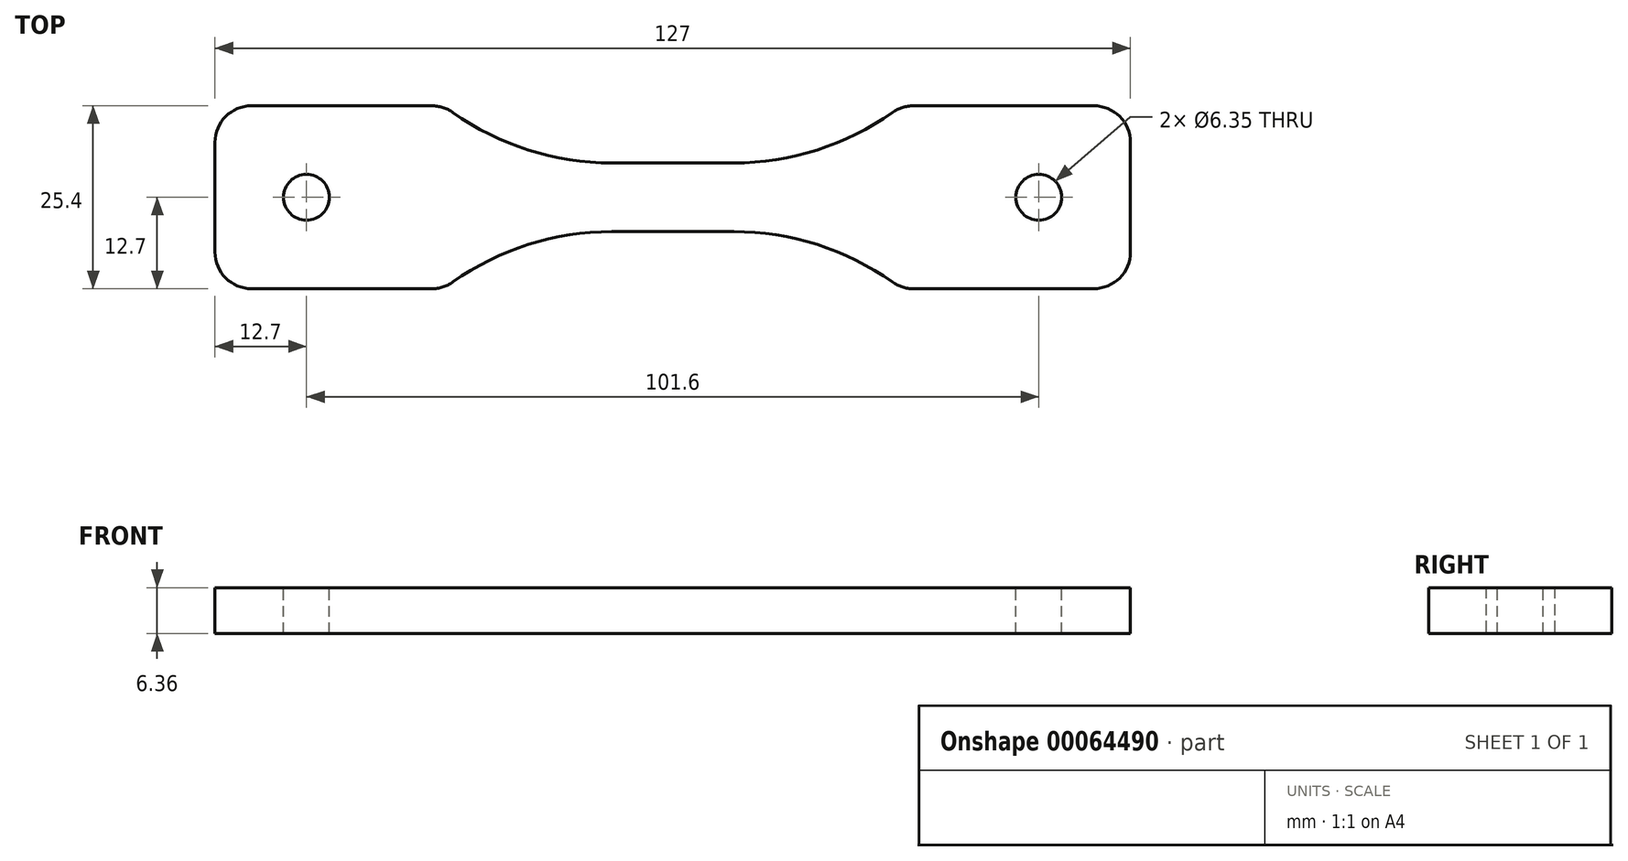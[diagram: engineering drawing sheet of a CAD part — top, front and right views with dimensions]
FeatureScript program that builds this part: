
annotation { "Feature Type Name" : "Feature", "Feature Type Description" : "" }
export const myFeature = defineFeature(function(context is Context, id is Id, definition is map)
    precondition{}
    {
        {
            var Q0;
            Q0=qCreatedBy(makeId("Top.planeOp"),FACE);
            var sketch = newSketch(context, id + "F0", { "sketchPlane" : qUnion([Q0])});
            skLineSegment(sketch, "E0.rect.bottom", {"start": v(63.5, -12.7) * mm, "end": v(-63.5, -12.7) * mm});
            skLineSegment(sketch, "E0.rect.top", {"start": v(63.5, 12.7) * mm, "end": v(-63.5, 12.7) * mm});
            skLineSegment(sketch, "E0.rect.left", {"start": v(63.5, -12.7) * mm, "end": v(63.5, 12.7) * mm});
            skLineSegment(sketch, "E0.rect.right", {"start": v(-63.5, -12.7) * mm, "end": v(-63.5, 12.7) * mm});
            skPoint(sketch, "E0.rect.middle", {"position": v(0, 0) * mm});
            skSolve(sketch);
        }
        {
            var Q0;
            Q0=makeQuery(id+"F0.imprint","IMPRINT",FACE,{"disambiguationData":[TD([[makeQuery(id+"F0.imprint","IMPRINT",EDGE,{"derivedFrom":sQuery(id+"F0.wireOp",EDGE,"E0.rect.bottom")}),-1.0]])]});
            extrude(context, id + "F1", {"entities" : qUnion([Q0]), "endBound" : BoundingType.SYMMETRIC, "depth" : 6.35 * mm});
        }
        {
            var Q0;
            Q0=makeQuery(id+"F1.opExtrude","CAP_FACE",FACE,{"disambiguationData":[OSD([sQuery(id+"F0.wireOp",EDGE,"E0.rect.bottom"),sQuery(id+"F0.wireOp",EDGE,"E0.rect.top"),sQuery(id+"F0.wireOp",EDGE,"E0.rect.left"),sQuery(id+"F0.wireOp",EDGE,"E0.rect.right")])],"isStart":false});
            var sketch = newSketch(context, id + "F2", { "sketchPlane" : qUnion([Q0])});
            skLineSegment(sketch, "E1", {"start": v(0, 50.7) * mm, "end": v(0, -34.35) * mm, "construction": true});
            skLineSegment(sketch, "E2.rect.bottom", {"start": v(31.75, 12.7) * mm, "end": v(-31.75, 12.7) * mm});
            skLineSegment(sketch, "E2.rect.top", {"start": v(31.75, 4.76) * mm, "end": v(-31.75, 4.76) * mm});
            skLineSegment(sketch, "E2.rect.left", {"start": v(31.75, 12.7) * mm, "end": v(31.75, 4.76) * mm});
            skLineSegment(sketch, "E2.rect.right", {"start": v(-31.75, 12.7) * mm, "end": v(-31.75, 4.76) * mm});
            skPoint(sketch, "E2.rect.middle", {"position": v(0, 8.73) * mm});
            skLineSegment(sketch, "E3", {"start": v(-70.63, 0) * mm, "end": v(74, 0) * mm, "construction": true});
            skPoint(sketch, "E3.endSnap0", {"position": v(-63.5, 0) * mm});
            skLineSegment(sketch, "E4.MirrorCS", {"start": v(-31.75, -12.7) * mm, "end": v(-31.75, -4.76) * mm});
            skPoint(sketch, "E5.MirrorP", {"position": v(0, -8.73) * mm});
            skLineSegment(sketch, "E6.MirrorCS", {"start": v(31.75, -12.7) * mm, "end": v(-31.75, -12.7) * mm});
            skLineSegment(sketch, "E7.MirrorCS", {"start": v(31.75, -4.76) * mm, "end": v(-31.75, -4.76) * mm});
            skLineSegment(sketch, "E8.MirrorCS", {"start": v(31.75, -12.7) * mm, "end": v(31.75, -4.76) * mm});
            skSolve(sketch);
        }
        {
            var Q0;
            Q0 = qSketchRegion(id + "F2", true);
            extrude(context, id + "F3", {"entities" : qUnion([Q0]), "operationType" : NewBodyOperationType.REMOVE, "oppositeDirection" : true, "depth" : 25.4 * mm});
        }
        {
            var Q0;
            Q0=makeQuery(id+"F3.boolean.opBoolean","COPY",EDGE,{"derivedFrom":makeQuery(id+"F3.opExtrude","SWEPT_EDGE",EDGE,{"disambiguationData":[OSD([sQuery(id+"F2.wireOp",EDGE,"E2.rect.top"),sQuery(id+"F2.wireOp",EDGE,"E2.rect.right")])]})});
            var Q1;
            Q1=makeQuery(id+"F3.boolean.opBoolean","COPY",EDGE,{"derivedFrom":makeQuery(id+"F3.opExtrude","SWEPT_EDGE",EDGE,{"disambiguationData":[OSD([sQuery(id+"F2.wireOp",EDGE,"E2.rect.top"),sQuery(id+"F2.wireOp",EDGE,"E2.rect.left")])]})});
            var Q2;
            Q2=makeQuery(id+"F3.boolean.opBoolean","COPY",EDGE,{"derivedFrom":makeQuery(id+"F3.opExtrude","SWEPT_EDGE",EDGE,{"disambiguationData":[OSD([sQuery(id+"F2.wireOp",EDGE,"E7.MirrorCS"),sQuery(id+"F2.wireOp",EDGE,"E8.MirrorCS")])]})});
            var Q3;
            Q3=makeQuery(id+"F3.boolean.opBoolean","COPY",EDGE,{"derivedFrom":makeQuery(id+"F3.opExtrude","SWEPT_EDGE",EDGE,{"disambiguationData":[OSD([sQuery(id+"F2.wireOp",EDGE,"E4.MirrorCS"),sQuery(id+"F2.wireOp",EDGE,"E7.MirrorCS")])]})});
            fillet(context, id + "F4", {"entities" : qUnion([Q0, Q1, Q2, Q3]), "radius" : 38.1 * mm, "tangentPropagation" : true, "allowEdgeOverflow" : false});
        }
        {
            var Q0;
            Q0=makeQuery(id+"F1.opExtrude","SWEPT_EDGE",EDGE,{"disambiguationData":[OSD([sQuery(id+"F0.wireOp",EDGE,"E0.rect.top"),sQuery(id+"F0.wireOp",EDGE,"E0.rect.right")])]});
            var Q1;
            {var subQ0=sQuery(id+"F0.wireOp",EDGE,"E0.rect.right");var subQ2=sQuery(id+"F0.wireOp",EDGE,"E0.rect.top");var subQ4=sQuery(id+"F2.wireOp",EDGE,"E2.rect.right");Q1=makeQuery(id+"F4.opFillet","BLEND_EDGE",EDGE,{"blendedFrom":[makeQuery(id+"F3.boolean.opBoolean","COPY",EDGE,{"derivedFrom":makeQuery(id+"F3.opExtrude","SWEPT_EDGE",EDGE,{"disambiguationData":[OSD([sQuery(id+"F2.wireOp",EDGE,"E2.rect.top"),subQ4])]})}),makeQuery(id+"F3.boolean.opBoolean","SPLIT",FACE,{"disambiguationData":[TD([makeQuery(id+"F1.opExtrude","SWEPT_FACE",FACE,{"disambiguationData":[OSD([subQ0])]})])],"derivedFrom":makeQuery(id+"F1.opExtrude","SWEPT_FACE",FACE,{"disambiguationData":[OSD([subQ2])]})})],"blendedInto":[makeQuery(id+"F3.boolean.opBoolean","SPLIT",FACE,{"disambiguationData":[TD([makeQuery(id+"F1.opExtrude","SWEPT_FACE",FACE,{"disambiguationData":[OSD([subQ0])]})])],"derivedFrom":makeQuery(id+"F1.opExtrude","SWEPT_FACE",FACE,{"disambiguationData":[OSD([subQ2])]})})]});}
            var Q2;
            Q2=makeQuery(id+"F1.opExtrude","SWEPT_EDGE",EDGE,{"disambiguationData":[OSD([sQuery(id+"F0.wireOp",EDGE,"E0.rect.bottom"),sQuery(id+"F0.wireOp",EDGE,"E0.rect.right")])]});
            var Q3;
            {var subQ0=sQuery(id+"F0.wireOp",EDGE,"E0.rect.right");var subQ3=sQuery(id+"F0.wireOp",EDGE,"E0.rect.bottom");var subQ4=sQuery(id+"F2.wireOp",EDGE,"E4.MirrorCS");Q3=makeQuery(id+"F4.opFillet","BLEND_EDGE",EDGE,{"blendedFrom":[makeQuery(id+"F3.boolean.opBoolean","COPY",EDGE,{"derivedFrom":makeQuery(id+"F3.opExtrude","SWEPT_EDGE",EDGE,{"disambiguationData":[OSD([subQ4,sQuery(id+"F2.wireOp",EDGE,"E7.MirrorCS")])]})}),makeQuery(id+"F3.boolean.opBoolean","SPLIT",FACE,{"disambiguationData":[TD([makeQuery(id+"F1.opExtrude","SWEPT_FACE",FACE,{"disambiguationData":[OSD([subQ0])]})])],"derivedFrom":makeQuery(id+"F1.opExtrude","SWEPT_FACE",FACE,{"disambiguationData":[OSD([subQ3])]})})],"blendedInto":[makeQuery(id+"F3.boolean.opBoolean","SPLIT",FACE,{"disambiguationData":[TD([makeQuery(id+"F1.opExtrude","SWEPT_FACE",FACE,{"disambiguationData":[OSD([subQ0])]})])],"derivedFrom":makeQuery(id+"F1.opExtrude","SWEPT_FACE",FACE,{"disambiguationData":[OSD([subQ3])]})})]});}
            var Q4;
            {var subQ1=sQuery(id+"F0.wireOp",EDGE,"E0.rect.left");var subQ3=sQuery(id+"F0.wireOp",EDGE,"E0.rect.bottom");var subQ4=sQuery(id+"F2.wireOp",EDGE,"E8.MirrorCS");Q4=makeQuery(id+"F4.opFillet","BLEND_EDGE",EDGE,{"blendedFrom":[makeQuery(id+"F3.boolean.opBoolean","COPY",EDGE,{"derivedFrom":makeQuery(id+"F3.opExtrude","SWEPT_EDGE",EDGE,{"disambiguationData":[OSD([sQuery(id+"F2.wireOp",EDGE,"E7.MirrorCS"),subQ4])]})}),makeQuery(id+"F3.boolean.opBoolean","SPLIT",FACE,{"disambiguationData":[TD([makeQuery(id+"F1.opExtrude","SWEPT_FACE",FACE,{"disambiguationData":[OSD([subQ1])]})])],"derivedFrom":makeQuery(id+"F1.opExtrude","SWEPT_FACE",FACE,{"disambiguationData":[OSD([subQ3])]})})],"blendedInto":[makeQuery(id+"F3.boolean.opBoolean","SPLIT",FACE,{"disambiguationData":[TD([makeQuery(id+"F1.opExtrude","SWEPT_FACE",FACE,{"disambiguationData":[OSD([subQ1])]})])],"derivedFrom":makeQuery(id+"F1.opExtrude","SWEPT_FACE",FACE,{"disambiguationData":[OSD([subQ3])]})})]});}
            var Q5;
            Q5=makeQuery(id+"F1.opExtrude","SWEPT_EDGE",EDGE,{"disambiguationData":[OSD([sQuery(id+"F0.wireOp",EDGE,"E0.rect.bottom"),sQuery(id+"F0.wireOp",EDGE,"E0.rect.left")])]});
            var Q6;
            Q6=makeQuery(id+"F1.opExtrude","SWEPT_EDGE",EDGE,{"disambiguationData":[OSD([sQuery(id+"F0.wireOp",EDGE,"E0.rect.top"),sQuery(id+"F0.wireOp",EDGE,"E0.rect.left")])]});
            var Q7;
            {var subQ1=sQuery(id+"F0.wireOp",EDGE,"E0.rect.left");var subQ2=sQuery(id+"F0.wireOp",EDGE,"E0.rect.top");var subQ4=sQuery(id+"F2.wireOp",EDGE,"E2.rect.left");Q7=makeQuery(id+"F4.opFillet","BLEND_EDGE",EDGE,{"blendedFrom":[makeQuery(id+"F3.boolean.opBoolean","COPY",EDGE,{"derivedFrom":makeQuery(id+"F3.opExtrude","SWEPT_EDGE",EDGE,{"disambiguationData":[OSD([sQuery(id+"F2.wireOp",EDGE,"E2.rect.top"),subQ4])]})}),makeQuery(id+"F3.boolean.opBoolean","SPLIT",FACE,{"disambiguationData":[TD([makeQuery(id+"F1.opExtrude","SWEPT_FACE",FACE,{"disambiguationData":[OSD([subQ1])]})])],"derivedFrom":makeQuery(id+"F1.opExtrude","SWEPT_FACE",FACE,{"disambiguationData":[OSD([subQ2])]})})],"blendedInto":[makeQuery(id+"F3.boolean.opBoolean","SPLIT",FACE,{"disambiguationData":[TD([makeQuery(id+"F1.opExtrude","SWEPT_FACE",FACE,{"disambiguationData":[OSD([subQ1])]})])],"derivedFrom":makeQuery(id+"F1.opExtrude","SWEPT_FACE",FACE,{"disambiguationData":[OSD([subQ2])]})})]});}
            fillet(context, id + "F5", {"entities" : qUnion([Q0, Q1, Q2, Q3, Q4, Q5, Q6, Q7]), "radius" : 5.08 * mm, "tangentPropagation" : true, "allowEdgeOverflow" : false});
        }
        {
            var Q0;
            Q0=makeQuery(id+"F1.opExtrude","CAP_FACE",FACE,{"disambiguationData":[OSD([sQuery(id+"F0.wireOp",EDGE,"E0.rect.bottom"),sQuery(id+"F0.wireOp",EDGE,"E0.rect.top"),sQuery(id+"F0.wireOp",EDGE,"E0.rect.left"),sQuery(id+"F0.wireOp",EDGE,"E0.rect.right")])],"isStart":false});
            var sketch = newSketch(context, id + "F6", { "sketchPlane" : qUnion([Q0])});
            skCircle(sketch, "E9", {"center": v(-50.8, 0) * mm, "radius": 3.18 * mm});
            skLineSegment(sketch, "E10", {"start": v(0, 26.4) * mm, "end": v(0, -30.32) * mm, "construction": true});
            skCircle(sketch, "E11.MirrorC", {"center": v(50.8, 0) * mm, "radius": 3.18 * mm});
            skSolve(sketch);
        }
        {
            var Q0;
            Q0 = qSketchRegion(id + "F6", true);
            extrude(context, id + "F7", {"entities" : qUnion([Q0]), "operationType" : NewBodyOperationType.REMOVE, "oppositeDirection" : true, "depth" : 25.4 * mm});
        }
    });
